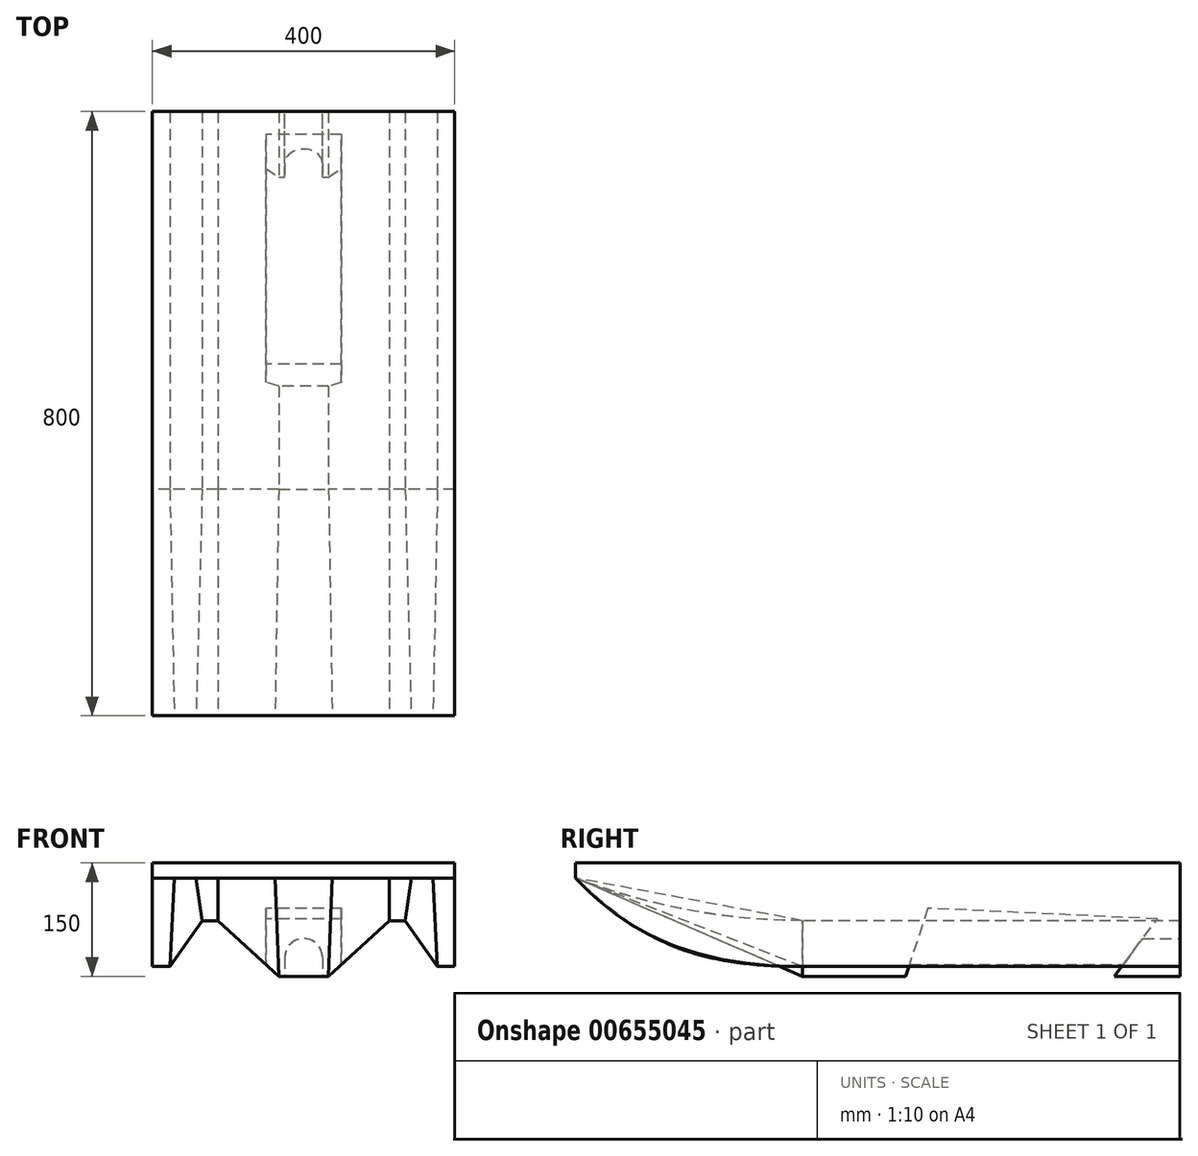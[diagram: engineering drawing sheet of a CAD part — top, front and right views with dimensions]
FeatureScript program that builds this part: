
annotation { "Feature Type Name" : "Feature", "Feature Type Description" : "" }
export const myFeature = defineFeature(function(context is Context, id is Id, definition is map)
    precondition{}
    {
        {
            assignVariable(context, id + "F0", {"name" : "Length", "anyValue" : 800});
        }
        {
            var Q0;
            Q0=qCreatedBy(makeId("Front.planeOp"),FACE);
            var sketch = newSketch(context, id + "F1", { "sketchPlane" : qUnion([Q0])});
            skLineSegment(sketch, "E0", {"start": v(-33, -23) * mm, "end": v(-113.45, 50.73) * mm});
            skLineSegment(sketch, "E1", {"start": v(-113.45, 50.73) * mm, "end": v(-134.23, 50.73) * mm});
            skLineSegment(sketch, "E2", {"start": v(-134.23, 50.73) * mm, "end": v(-177.04, -10.14) * mm});
            skLineSegment(sketch, "E3", {"start": v(-177.04, -10.14) * mm, "end": v(-200, -10.14) * mm});
            skLineSegment(sketch, "E4", {"start": v(-200, -10.14) * mm, "end": v(-200, 127) * mm});
            skLineSegment(sketch, "E5", {"start": v(-200, 127) * mm, "end": v(200, 127) * mm});
            skLineSegment(sketch, "E6", {"start": v(200, 127) * mm, "end": v(200, -10.14) * mm});
            skLineSegment(sketch, "E7", {"start": v(200, -10.14) * mm, "end": v(177.04, -10.14) * mm});
            skLineSegment(sketch, "E8", {"start": v(177.04, -10.14) * mm, "end": v(134.23, 50.73) * mm});
            skLineSegment(sketch, "E9", {"start": v(134.23, 50.73) * mm, "end": v(113.45, 50.73) * mm});
            skLineSegment(sketch, "E10", {"start": v(113.45, 50.73) * mm, "end": v(33, -23) * mm});
            skLineSegment(sketch, "E11", {"start": v(33, -23) * mm, "end": v(-33, -23) * mm});
            skSolve(sketch);
        }
        {
            var Q0;
            Q0=qCreatedBy(makeId("Front.planeOp"),FACE);
            cPlane(context, id + "F2", {"entities" : qUnion([Q0]), "cplaneType" : CPlaneType.OFFSET, "offset" : (getVariable(context, 'Length')) * mm, "width" : 150 * mm, "height" : 150 * mm});
        }
        {
            var Q0;
            Q0=qCreatedBy(makeId("Front.planeOp"),FACE);
            cPlane(context, id + "F3", {"entities" : qUnion([Q0]), "cplaneType" : CPlaneType.OFFSET, "offset" : 500 * mm, "width" : 150 * mm, "height" : 150 * mm});
        }
        {
            var Q0;
            Q0=qCreatedBy(id+"F3.planeOp",FACE);
            var sketch = newSketch(context, id + "F4", { "sketchPlane" : qUnion([Q0])});
            skLineSegment(sketch, "E12.0", {"start": v(-33, -23) * mm, "end": v(-113.45, 50.73) * mm});
            skLineSegment(sketch, "E12.2", {"start": v(-200, 127) * mm, "end": v(200, 127) * mm});
            skLineSegment(sketch, "E12.3", {"start": v(-200, -10.14) * mm, "end": v(-200, 127) * mm});
            skLineSegment(sketch, "E12.4", {"start": v(-177.04, -10.14) * mm, "end": v(-200, -10.14) * mm});
            skLineSegment(sketch, "E12.5", {"start": v(-113.45, 50.73) * mm, "end": v(-134.23, 50.73) * mm});
            skLineSegment(sketch, "E12.6", {"start": v(200, 127) * mm, "end": v(200, -10.14) * mm});
            skLineSegment(sketch, "E12.7", {"start": v(200, -10.14) * mm, "end": v(177.04, -10.14) * mm});
            skLineSegment(sketch, "E12.8", {"start": v(-134.23, 50.73) * mm, "end": v(-177.04, -10.14) * mm});
            skLineSegment(sketch, "E12.9", {"start": v(177.04, -10.14) * mm, "end": v(134.23, 50.73) * mm});
            skLineSegment(sketch, "E12.10", {"start": v(134.23, 50.73) * mm, "end": v(113.45, 50.73) * mm});
            skLineSegment(sketch, "E12.11", {"start": v(113.45, 50.73) * mm, "end": v(33, -23) * mm});
            skLineSegment(sketch, "E13", {"start": v(-33, -23) * mm, "end": v(33, -23) * mm});
            skSolve(sketch);
        }
        {
            var Q0;
            Q0=qCreatedBy(id+"F2.planeOp",FACE);
            var sketch = newSketch(context, id + "F5", { "sketchPlane" : qUnion([Q0])});
            skLineSegment(sketch, "E14.0", {"start": v(-200, 127) * mm, "end": v(200, 127) * mm});
            skLineSegment(sketch, "E15", {"start": v(-200, 127) * mm, "end": v(-200, 107) * mm});
            skLineSegment(sketch, "E16", {"start": v(-200, 107) * mm, "end": v(200, 107) * mm});
            skLineSegment(sketch, "E17", {"start": v(200, 107) * mm, "end": v(200, 127) * mm});
            skPoint(sketch, "E18.0", {"position": v(-177.04, -10.14) * mm});
            skPoint(sketch, "E19.0", {"position": v(-134.23, 50.73) * mm});
            skPoint(sketch, "E20.0", {"position": v(-113.45, 50.73) * mm});
            skPoint(sketch, "E21.0", {"position": v(-33, -23) * mm});
            skPoint(sketch, "E22.0", {"position": v(33, -23) * mm});
            skPoint(sketch, "E23.0", {"position": v(113.45, 50.73) * mm});
            skPoint(sketch, "E24.0", {"position": v(134.23, 50.73) * mm});
            skPoint(sketch, "E25.0", {"position": v(177.04, -10.14) * mm});
            skPoint(sketch, "E26", {"position": v(-177.04, 107) * mm});
            skPoint(sketch, "E27", {"position": v(-134.23, 107) * mm});
            skPoint(sketch, "E28", {"position": v(-113.45, 107) * mm});
            skPoint(sketch, "E29", {"position": v(-33, 107) * mm});
            skPoint(sketch, "E30", {"position": v(33, 107) * mm});
            skPoint(sketch, "E31", {"position": v(113.45, 107) * mm});
            skPoint(sketch, "E32", {"position": v(134.23, 107) * mm});
            skPoint(sketch, "E33", {"position": v(177.04, 107) * mm});
            skPoint(sketch, "E34", {"position": v(-177.04, 127) * mm});
            skPoint(sketch, "E35", {"position": v(-134.23, 127) * mm});
            skPoint(sketch, "E36", {"position": v(-113.45, 127) * mm});
            skPoint(sketch, "E37", {"position": v(-33, 127) * mm});
            skPoint(sketch, "E38", {"position": v(33, 127) * mm});
            skPoint(sketch, "E39", {"position": v(113.45, 127) * mm});
            skPoint(sketch, "E40", {"position": v(134.23, 127) * mm});
            skPoint(sketch, "E41", {"position": v(177.04, 127) * mm});
            skSolve(sketch);
        }
        {
            var Q0;
            Q0=sQuery(id+"F1.wireOp",VERTEX,"E7.start");
            var Q1;
            Q1=sQuery(id+"F1.wireOp",VERTEX,"E4.start");
            var Q2;
            Q2=sQuery(id+"F4.wireOp",VERTEX,"E12.4.end");
            cPlane(context, id + "F6", {"entities" : qUnion([Q0, Q1, Q2]), "cplaneType" : CPlaneType.THREE_POINT, "offset" : 25 * mm, "width" : 150 * mm, "height" : 150 * mm});
        }
        {
            var Q0;
            Q0=qCreatedBy(id+"F6.planeOp",FACE);
            var sketch = newSketch(context, id + "F7", { "sketchPlane" : qUnion([Q0])});
            skLineSegment(sketch, "E42", {"start": v(200, 500) * mm, "end": v(200, 0) * mm});
            skLineSegment(sketch, "E43", {"start": v(177.04, 500) * mm, "end": v(177.04, 0) * mm});
            skLineSegment(sketch, "E44", {"start": v(-177.04, 500) * mm, "end": v(-177.04, 0) * mm});
            skLineSegment(sketch, "E45", {"start": v(-200, 500) * mm, "end": v(-200, 0) * mm});
            skSolve(sketch);
        }
        {
            var Q0;
            Q0=makeQuery(id+"F1.imprint","IMPRINT",FACE,{"disambiguationData":[TD([[makeQuery(id+"F1.imprint","IMPRINT",EDGE,{"derivedFrom":sQuery(id+"F1.wireOp",EDGE,"E0")}),-1.0]])]});
            var Q1;
            Q1=makeQuery(id+"F4.imprint","IMPRINT",FACE,{"disambiguationData":[TD([[makeQuery(id+"F4.imprint","IMPRINT",EDGE,{"derivedFrom":sQuery(id+"F4.wireOp",EDGE,"E12.0")}),-1.0]])]});
            loft(context, id + "F8", {"sheetProfilesArray" : [{ "sheetProfileEntities" : qUnion([Q0]) }, { "sheetProfileEntities" : qUnion([Q1]) }]});
        }
        {
            var Q0;
            Q0=sQuery(id+"F7.wireOp",VERTEX,"E42.start");
            var Q1;
            Q1=makeQuery(id+"F8.opLoft","MID_CAP_VERTEX",VERTEX,{"disambiguationData":[OSD([sQuery(id+"F4.wireOp",EDGE,"E12.2"),sQuery(id+"F4.wireOp",EDGE,"E12.6")])],"capPos":1.0});
            var Q2;
            Q2=sQuery(id+"F5.wireOp",VERTEX,"E14.0.end");
            cPlane(context, id + "F9", {"entities" : qUnion([Q0, Q1, Q2]), "cplaneType" : CPlaneType.THREE_POINT, "offset" : 25 * mm, "width" : 150 * mm, "height" : 150 * mm});
        }
        {
            var Q0;
            Q0=qCreatedBy(id+"F9.planeOp",FACE);
            var sketch = newSketch(context, id + "F10", { "sketchPlane" : qUnion([Q0])});
            skFitSpline(sketch, "E46", {"points": [v(500, -10.14) * mm, v(800, 107) * mm], "startDerivative": vector(465.15, 0) * mm, "endDerivative": vector(180.82, 195.2) * mm});
            skSolve(sketch);
        }
        {
            var Q0;
            Q0=sQuery(id+"F7.wireOp",VERTEX,"E45.start");
            var Q1;
            Q1=makeQuery(id+"F8.opLoft","MID_CAP_VERTEX",VERTEX,{"disambiguationData":[OSD([sQuery(id+"F4.wireOp",EDGE,"E12.2"),sQuery(id+"F4.wireOp",EDGE,"E12.3")])],"capPos":1.0});
            var Q2;
            Q2=sQuery(id+"F5.wireOp",VERTEX,"E14.0.start");
            cPlane(context, id + "F11", {"entities" : qUnion([Q0, Q1, Q2]), "cplaneType" : CPlaneType.THREE_POINT, "offset" : 25 * mm, "width" : 150 * mm, "height" : 150 * mm});
        }
        {
            var Q0;
            Q0=qCreatedBy(id+"F11.planeOp",FACE);
            var sketch = newSketch(context, id + "F12", { "sketchPlane" : qUnion([Q0])});
            skFitSpline(sketch, "E47", {"points": [v(500, -10.14) * mm, v(800, 107) * mm], "startDerivative": vector(468.04, 0) * mm, "endDerivative": vector(238.55, 225.51) * mm});
            skSolve(sketch);
        }
        {
            var Q0;
            Q0=makeQuery(id+"F8.opLoft","MID_CAP_VERTEX",VERTEX,{"disambiguationData":[OSD([sQuery(id+"F4.wireOp",EDGE,"E12.10"),sQuery(id+"F4.wireOp",EDGE,"E12.11")])],"capPos":1.0});
            var Q1;
            Q1=sQuery(id+"F5.wireOp",VERTEX,"E31");
            var Q2;
            Q2=sQuery(id+"F5.wireOp",VERTEX,"E39");
            cPlane(context, id + "F13", {"entities" : qUnion([Q0, Q1, Q2]), "cplaneType" : CPlaneType.THREE_POINT, "offset" : 25 * mm, "width" : 150 * mm, "height" : 150 * mm});
        }
        {
            var Q0;
            Q0=qCreatedBy(id+"F13.planeOp",FACE);
            var sketch = newSketch(context, id + "F14", { "sketchPlane" : qUnion([Q0])});
            skFitSpline(sketch, "E48", {"points": [v(-500, 50.73) * mm, v(-800, 107) * mm], "startDerivative": vector(-298.9, 0) * mm, "endDerivative": vector(-312.25, 117.8) * mm});
            skSolve(sketch);
        }
        {
            var Q0;
            Q0=sQuery(id+"F5.wireOp",VERTEX,"E28");
            var Q1;
            Q1=sQuery(id+"F5.wireOp",VERTEX,"E36");
            var Q2;
            Q2=makeQuery(id+"F8.opLoft","MID_CAP_VERTEX",VERTEX,{"disambiguationData":[OSD([sQuery(id+"F4.wireOp",EDGE,"E12.0"),sQuery(id+"F4.wireOp",EDGE,"E12.5")])],"capPos":1.0});
            cPlane(context, id + "F15", {"entities" : qUnion([Q0, Q1, Q2]), "cplaneType" : CPlaneType.THREE_POINT, "offset" : 25 * mm, "width" : 150 * mm, "height" : 150 * mm});
        }
        {
            var Q0;
            Q0=qCreatedBy(id+"F15.planeOp",FACE);
            var sketch = newSketch(context, id + "F16", { "sketchPlane" : qUnion([Q0])});
            skFitSpline(sketch, "E49", {"points": [v(-500, 50.73) * mm, v(-800, 107) * mm], "startDerivative": vector(-289.19, 0) * mm, "endDerivative": vector(-298.9, 115.37) * mm});
            skSolve(sketch);
        }
        {
            var Q1;
            Q1 = qSketchRegion(id + "F4", true);
            var Q2;
            Q2 = qSketchRegion(id + "F5", true);
            var Q3;
            Q3=sQuery(id+"F10.wireOp",EDGE,"E46");
            var Q4;
            Q4=sQuery(id+"F14.wireOp",EDGE,"E48");
            var Q5;
            Q5=sQuery(id+"F16.wireOp",EDGE,"E49");
            var Q6;
            Q6=sQuery(id+"F12.wireOp",EDGE,"E47");
            loft(context, id + "F17", {"operationType" : NewBodyOperationType.ADD, "addGuides" : true, "sheetProfilesArray" : [{ "sheetProfileEntities" : qUnion([Q1]) }, { "sheetProfileEntities" : qUnion([Q2]) }], "guidesArray" : [{ "guideEntities" : qUnion([Q3]), "guideDerivativeType" : LoftGuideDerivativeType.DEFAULT, "guideDerivativeMagnitude" : 1 }, { "guideEntities" : qUnion([Q4]), "guideDerivativeType" : LoftGuideDerivativeType.DEFAULT, "guideDerivativeMagnitude" : 1 }, { "guideEntities" : qUnion([Q5]), "guideDerivativeType" : LoftGuideDerivativeType.DEFAULT, "guideDerivativeMagnitude" : 1 }, { "guideEntities" : qUnion([Q6]), "guideDerivativeType" : LoftGuideDerivativeType.DEFAULT, "guideDerivativeMagnitude" : 1 }]});
        }
        {
            var Q0;
            Q0=makeQuery(id+"F8.opLoft","CAP_FACE",FACE,{"disambiguationData":[OSD([makeQuery(id+"F1.imprint","IMPRINT",FACE,{"disambiguationData":[TD([[makeQuery(id+"F1.imprint","IMPRINT",EDGE,{"derivedFrom":sQuery(id+"F1.wireOp",EDGE,"E0")}),-1.0]])]})])],"isStart":true});
            var sketch = newSketch(context, id + "F18", { "sketchPlane" : qUnion([Q0])});
            skCircle(sketch, "E50", {"center": v(0, 2) * mm, "radius": 20 * mm, "construction": true});
            skArc(sketch, "E51", {"start": v(-25, 2) * mm, "mid": v(0, 27) * mm, "end": v(25, 2) * mm});
            skLineSegment(sketch, "E52", {"start": v(-25, 2) * mm, "end": v(-25, -23) * mm});
            skLineSegment(sketch, "E53", {"start": v(25, 2) * mm, "end": v(25, -23) * mm});
            skLineSegment(sketch, "E54", {"start": v(25, -23) * mm, "end": v(-25, -23) * mm});
            skSolve(sketch);
        }
        {
            var Q0;
            Q0 = qSketchRegion(id + "F18", true);
            extrude(context, id + "F19", {"entities" : qUnion([Q0]), "oppositeDirection" : true, "depth" : 180 * mm, "offsetDistance" : 25 * mm});
        }
        {
            var Q0;
            Q0=qCreatedBy(makeId("Right.planeOp"),FACE);
            var sketch = newSketch(context, id + "F20", { "sketchPlane" : qUnion([Q0])});
            skLineSegment(sketch, "E55", {"start": v(-97.51, -37.08) * mm, "end": v(-30.22, 52.93) * mm});
            skLineSegment(sketch, "E56", {"start": v(-30.22, 52.93) * mm, "end": v(-334.1, 67.07) * mm});
            skLineSegment(sketch, "E57", {"start": v(-334.1, 67.07) * mm, "end": v(-382.11, -80.37) * mm});
            skLineSegment(sketch, "E58", {"start": v(-382.11, -80.37) * mm, "end": v(-97.51, -37.08) * mm});
            skSolve(sketch);
        }
        {
            var Q0;
            Q0 = qSketchRegion(id + "F20", true);
            extrude(context, id + "F21", {"entities" : qUnion([Q0]), "operationType" : NewBodyOperationType.REMOVE, "endBound" : BoundingType.SYMMETRIC, "depth" : 100 * mm, "offsetDistance" : 25 * mm});
        }
        {
            var Q0;
            Q0=makeQuery(id+"F19.opExtrude","SWEPT_BODY",BODY,{"disambiguationData":[OSD([sQuery(id+"F18.wireOp",EDGE,"E51"),sQuery(id+"F18.wireOp",EDGE,"E52"),sQuery(id+"F18.wireOp",EDGE,"E53"),sQuery(id+"F18.wireOp",EDGE,"E54")])]});
            var Q1;
            Q1=makeQuery(id+"F8.opLoft","SWEPT_BODY",BODY,{"disambiguationData":[OSD([makeQuery(id+"F1.imprint","IMPRINT",FACE,{"disambiguationData":[TD([[makeQuery(id+"F1.imprint","IMPRINT",EDGE,{"derivedFrom":sQuery(id+"F1.wireOp",EDGE,"E0")}),-1.0]])]}),makeQuery(id+"F4.imprint","IMPRINT",FACE,{"disambiguationData":[TD([[makeQuery(id+"F4.imprint","IMPRINT",EDGE,{"derivedFrom":sQuery(id+"F4.wireOp",EDGE,"E12.0")}),-1.0]])]})])]});
            booleanBodies(context, id + "F22", {"operationType" : BooleanOperationType.SUBTRACTION, "tools" : qUnion([Q0]), "targets" : qUnion([Q1])});
        }
    });
